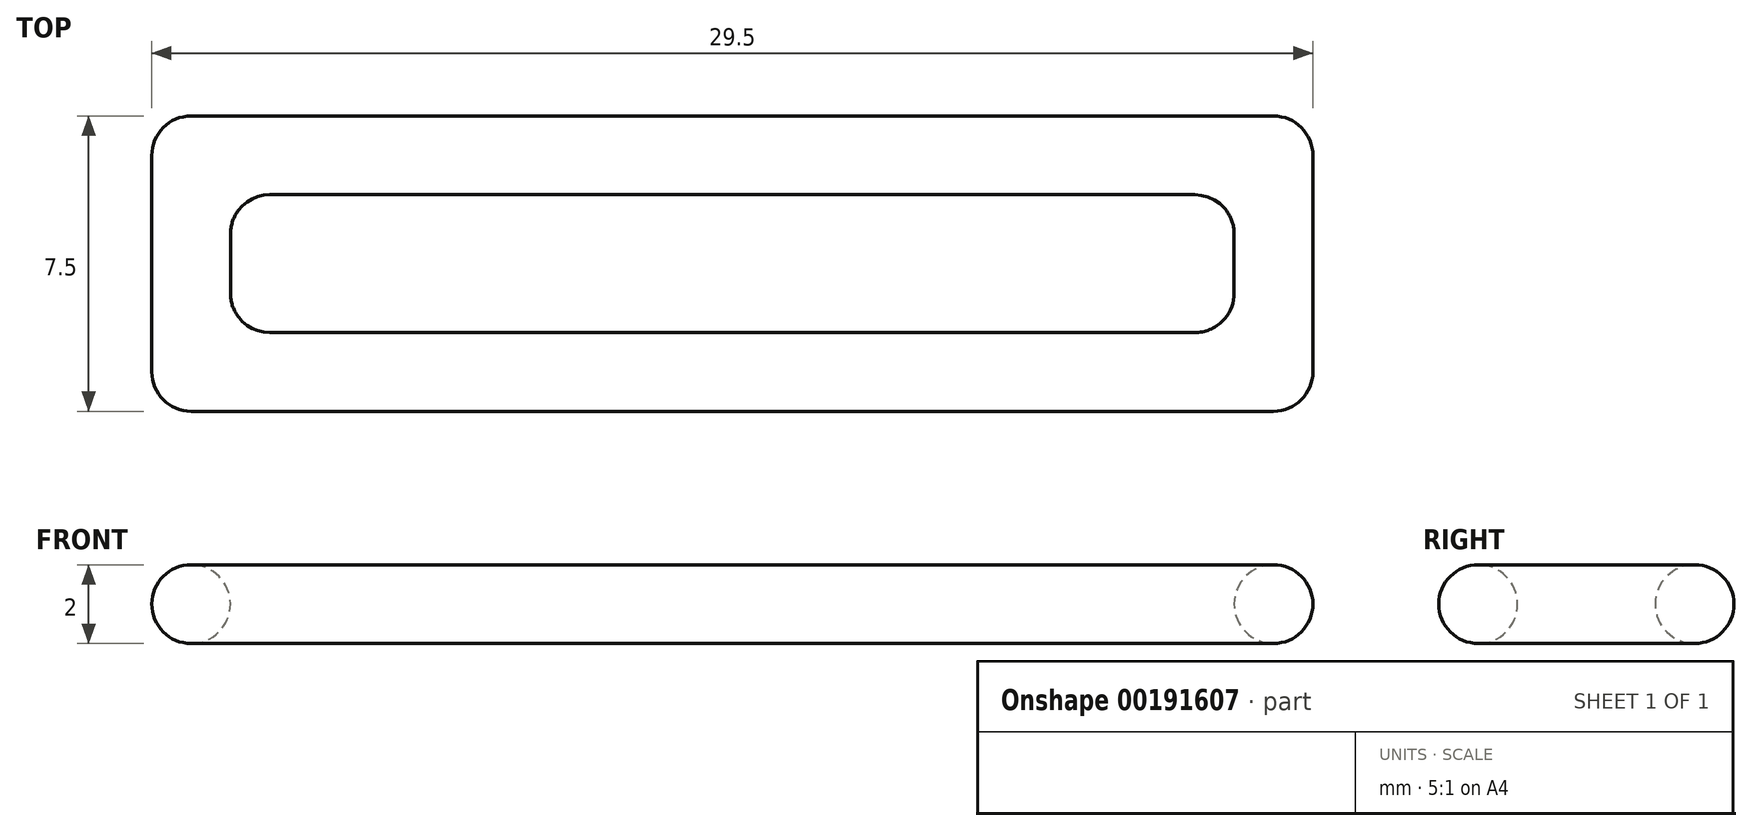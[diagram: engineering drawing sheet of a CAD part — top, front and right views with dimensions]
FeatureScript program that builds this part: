
annotation { "Feature Type Name" : "Feature", "Feature Type Description" : "" }
export const myFeature = defineFeature(function(context is Context, id is Id, definition is map)
    precondition{}
    {
        {
            var Q0;
            Q0=qCreatedBy(makeId("Top.planeOp"),FACE);
            var sketch = newSketch(context, id + "F0", { "sketchPlane" : qUnion([Q0])});
            skLineSegment(sketch, "E0.bottom", {"start": v(11.75, 1.75) * mm, "end": v(-11.75, 1.75) * mm});
            skLineSegment(sketch, "E0.top", {"start": v(11.75, -1.75) * mm, "end": v(-11.75, -1.75) * mm});
            skLineSegment(sketch, "E0.left", {"start": v(12.75, 0.75) * mm, "end": v(12.75, -0.75) * mm});
            skLineSegment(sketch, "E0.right", {"start": v(-12.75, 0.75) * mm, "end": v(-12.75, -0.75) * mm});
            skPoint(sketch, "E0.middle", {"position": v(0, 0) * mm});
            skLineSegment(sketch, "E1.0", {"start": v(-14.75, 2.75) * mm, "end": v(-14.75, -2.75) * mm});
            skLineSegment(sketch, "E1.1", {"start": v(13.75, 3.75) * mm, "end": v(-13.75, 3.75) * mm});
            skLineSegment(sketch, "E1.2", {"start": v(14.75, 2.75) * mm, "end": v(14.75, -2.75) * mm});
            skLineSegment(sketch, "E1.3", {"start": v(13.75, -3.75) * mm, "end": v(-13.75, -3.75) * mm});
            skPoint(sketch, "E2.visualSharp", {"position": v(-14.75, -3.75) * mm});
            skArc(sketch, "E2.filletArc", {"start": v(-14.75, -2.75) * mm, "mid": v(-14.46, -3.46) * mm, "end": v(-13.75, -3.75) * mm});
            skPoint(sketch, "E3.visualSharp", {"position": v(-14.75, 3.75) * mm});
            skArc(sketch, "E3.filletArc", {"start": v(-13.75, 3.75) * mm, "mid": v(-14.46, 3.46) * mm, "end": v(-14.75, 2.75) * mm});
            skPoint(sketch, "E4.visualSharp", {"position": v(14.75, 3.75) * mm});
            skArc(sketch, "E4.filletArc", {"start": v(14.75, 2.75) * mm, "mid": v(14.46, 3.46) * mm, "end": v(13.75, 3.75) * mm});
            skPoint(sketch, "E5.visualSharp", {"position": v(14.75, -3.75) * mm});
            skArc(sketch, "E5.filletArc", {"start": v(13.75, -3.75) * mm, "mid": v(14.46, -3.46) * mm, "end": v(14.75, -2.75) * mm});
            skPoint(sketch, "E6.visualSharp", {"position": v(12.75, -1.75) * mm});
            skArc(sketch, "E6.filletArc", {"start": v(11.75, -1.75) * mm, "mid": v(12.46, -1.46) * mm, "end": v(12.75, -0.75) * mm});
            skPoint(sketch, "E7.visualSharp", {"position": v(12.75, 1.75) * mm});
            skArc(sketch, "E7.filletArc", {"start": v(12.75, 0.75) * mm, "mid": v(12.46, 1.46) * mm, "end": v(11.75, 1.75) * mm});
            skPoint(sketch, "E8.visualSharp", {"position": v(-12.75, 1.75) * mm});
            skArc(sketch, "E8.filletArc", {"start": v(-11.75, 1.75) * mm, "mid": v(-12.46, 1.46) * mm, "end": v(-12.75, 0.75) * mm});
            skPoint(sketch, "E9.visualSharp", {"position": v(-12.75, -1.75) * mm});
            skArc(sketch, "E9.filletArc", {"start": v(-12.75, -0.75) * mm, "mid": v(-12.46, -1.46) * mm, "end": v(-11.75, -1.75) * mm});
            skSolve(sketch);
        }
        {
            var Q0;
            Q0=makeQuery(id+"F0.imprint","IMPRINT",FACE,{"disambiguationData":[TD([[makeQuery(id+"F0.imprint","IMPRINT",EDGE,{"derivedFrom":sQuery(id+"F0.wireOp",EDGE,"E0.bottom")}),-1.0]])]});
            extrude(context, id + "F1", {"entities" : qUnion([Q0]), "depth" : 2 * mm});
        }
        {
            var Q0;
            Q0=makeQuery(id+"F1.opExtrude","CAP_EDGE",EDGE,{"disambiguationData":[OSD([sQuery(id+"F0.wireOp",EDGE,"E0.bottom")])],"isStart":false});
            var Q1;
            Q1=makeQuery(id+"F1.opExtrude","CAP_EDGE",EDGE,{"disambiguationData":[OSD([sQuery(id+"F0.wireOp",EDGE,"E0.bottom")])],"isStart":true});
            var Q2;
            Q2=makeQuery(id+"F1.opExtrude","CAP_EDGE",EDGE,{"disambiguationData":[OSD([sQuery(id+"F0.wireOp",EDGE,"E1.1")])],"isStart":true});
            var Q3;
            Q3=makeQuery(id+"F1.opExtrude","CAP_EDGE",EDGE,{"disambiguationData":[OSD([sQuery(id+"F0.wireOp",EDGE,"E1.3")])],"isStart":false});
            fillet(context, id + "F2", {"entities" : qUnion([Q0, Q1, Q2, Q3]), "radius" : 1 * mm, "tangentPropagation" : true, "allowEdgeOverflow" : false});
        }
    });
